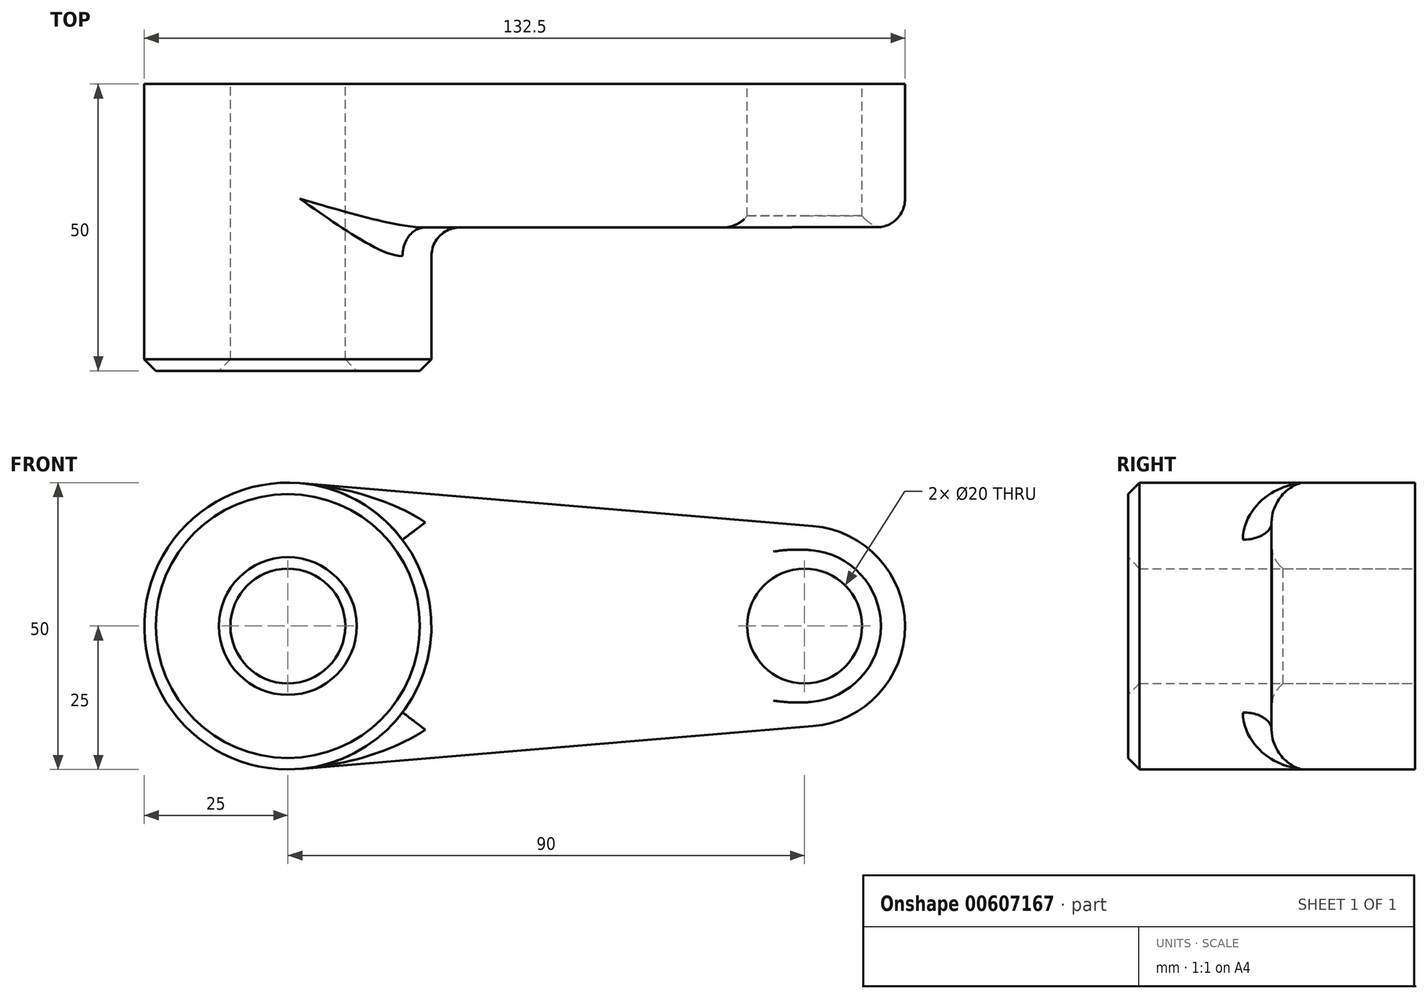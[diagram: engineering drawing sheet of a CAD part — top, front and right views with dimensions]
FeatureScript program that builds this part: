
annotation { "Feature Type Name" : "Feature", "Feature Type Description" : "" }
export const myFeature = defineFeature(function(context is Context, id is Id, definition is map)
    precondition{}
    {
        {
            var Q0;
            Q0=qCreatedBy(makeId("Front.planeOp"),FACE);
            var sketch = newSketch(context, id + "F0", { "sketchPlane" : qUnion([Q0])});
            skCircle(sketch, "E0", {"center": v(0, 0) * mm, "radius": 25 * mm});
            skCircle(sketch, "E1", {"center": v(90, 0) * mm, "radius": 17.5 * mm});
            skLineSegment(sketch, "E2", {"start": v(2.08, 24.91) * mm, "end": v(91.46, 17.44) * mm});
            skLineSegment(sketch, "E3", {"start": v(2.08, -24.91) * mm, "end": v(91.46, -17.44) * mm});
            skLineSegment(sketch, "E4", {"start": v(91.46, -17.44) * mm, "end": v(63.97, -19.74) * mm});
            skCircle(sketch, "E5", {"center": v(0, 0) * mm, "radius": 10 * mm});
            skCircle(sketch, "E6", {"center": v(90, 0) * mm, "radius": 10 * mm});
            skSolve(sketch);
        }
        {
            var Q0;
            Q0=makeQuery(id+"F0.imprint","IMPRINT",FACE,{"disambiguationData":[TD([[makeQuery(id+"F0.imprint","IMPRINT",EDGE,{"derivedFrom":sQuery(id+"F0.wireOp",EDGE,"E0")}),1.0]])]});
            var sketch = newSketch(context, id + "F1", { "sketchPlane" : qUnion([Q0])});
            skSolve(sketch);
        }
        {
            var Q0;
            Q0 = qSketchRegion(id + "F0", true);
            extrude(context, id + "F2", {"entities" : qUnion([Q0]), "depth" : 25 * mm, "offsetDistance" : 25 * mm});
        }
        {
            var Q0;
            Q0=makeQuery(id+"F1.imprint","IMPRINT",FACE,{"disambiguationData":[TD([[makeQuery(id+"F1.imprint","IMPRINT",EDGE,{"derivedFrom":makeQuery(id+"F0.imprint","IMPRINT",EDGE,{"derivedFrom":sQuery(id+"F0.wireOp",EDGE,"E5")})}),-1.0]])]});
            extrude(context, id + "F3", {"entities" : qUnion([Q0]), "operationType" : NewBodyOperationType.ADD, "depth" : 50 * mm, "offsetDistance" : 25 * mm});
        }
        {
            var Q0;
            Q0=makeQuery(id+"F3.opExtrude","CAP_EDGE",EDGE,{"disambiguationData":[OSD([sQuery(id+"F0.wireOp",EDGE,"E0")])],"isStart":false});
            var Q1;
            Q1=makeQuery(id+"F3.opExtrude","CAP_EDGE",EDGE,{"disambiguationData":[OSD([sQuery(id+"F0.wireOp",EDGE,"E5")])],"isStart":false});
            var Q2;
            Q2=makeQuery(id+"F2.opExtrude","CAP_EDGE",EDGE,{"disambiguationData":[OSD([sQuery(id+"F0.wireOp",EDGE,"E6")])],"isStart":false});
            chamfer(context, id + "F4", {"entities" : qUnion([Q0, Q1, Q2]), "width" : 2 * mm, "tangentPropagation" : true});
        }
        {
            var Q0;
            Q0=makeQuery(id+"F2.opExtrude","CAP_FACE",FACE,{"disambiguationData":[OSD([sQuery(id+"F0.wireOp",EDGE,"E0"),sQuery(id+"F0.wireOp",EDGE,"E1"),sQuery(id+"F0.wireOp",EDGE,"E2"),sQuery(id+"F0.wireOp",EDGE,"E3"),sQuery(id+"F0.wireOp",EDGE,"E4"),sQuery(id+"F0.wireOp",EDGE,"E5"),sQuery(id+"F0.wireOp",EDGE,"E6")])],"isStart":false});
            fillet(context, id + "F5", {"entities" : qUnion([Q0]), "radius" : 5 * mm, "tangentPropagation" : true, "allowEdgeOverflow" : false});
        }
    });
